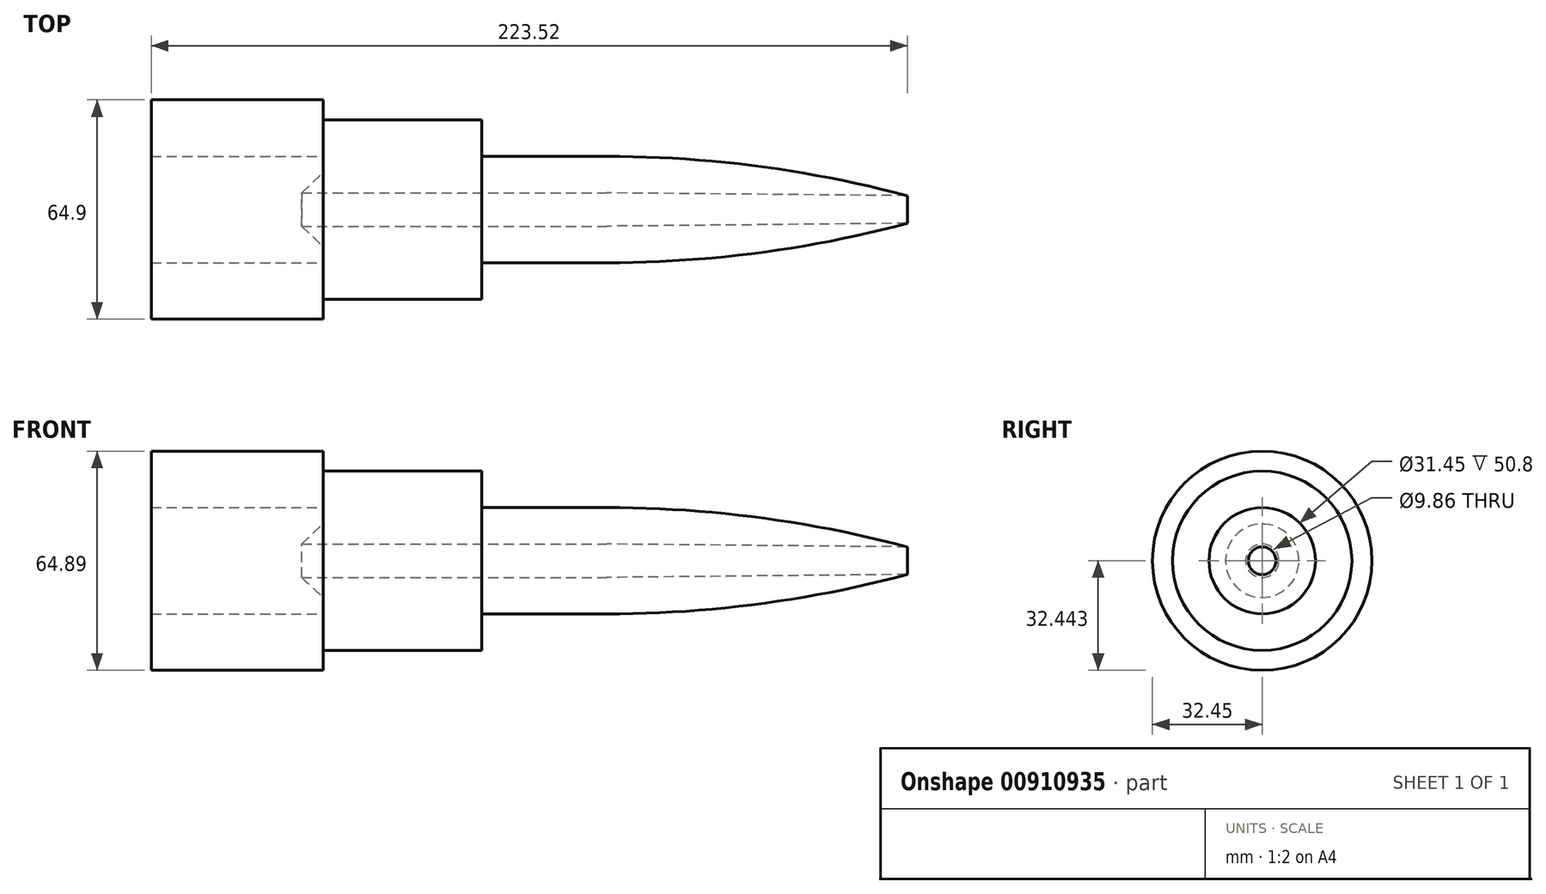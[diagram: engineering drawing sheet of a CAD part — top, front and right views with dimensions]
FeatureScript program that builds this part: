
annotation { "Feature Type Name" : "Feature", "Feature Type Description" : "" }
export const myFeature = defineFeature(function(context is Context, id is Id, definition is map)
    precondition{}
    {
        {
            var Q0;
            Q0=qCreatedBy(makeId("Front.planeOp"),FACE);
            var sketch = newSketch(context, id + "F0", { "sketchPlane" : qUnion([Q0])});
            skLineSegment(sketch, "E0.bottom", {"start": v(-57.4, 34.77) * mm, "end": v(-10.41, 34.77) * mm});
            skLineSegment(sketch, "E0.top", {"start": v(-57.4, 13.18) * mm, "end": v(-10.41, 13.18) * mm});
            skLineSegment(sketch, "E0.left", {"start": v(-57.4, 34.77) * mm, "end": v(-57.4, 13.18) * mm});
            skLineSegment(sketch, "E0.right", {"start": v(-10.41, 34.77) * mm, "end": v(-10.41, 13.18) * mm});
            skPoint(sketch, "E1.oppositeSnap0", {"position": v(-10.41, 23.98) * mm});
            skLineSegment(sketch, "E1.bottom", {"start": v(-10.41, 13.18) * mm, "end": v(26.41, 13.18) * mm});
            skLineSegment(sketch, "E1.top", {"start": v(-10.41, 23.98) * mm, "end": v(26.41, 23.98) * mm});
            skLineSegment(sketch, "E1.left", {"start": v(-10.41, 13.18) * mm, "end": v(-10.41, 23.98) * mm});
            skLineSegment(sketch, "E1.right", {"start": v(26.41, 13.18) * mm, "end": v(26.41, 23.98) * mm});
            skArc(sketch, "E2", {"start": v(26.41, 23.98) * mm, "mid": v(71.24, 21.06) * mm, "end": v(115.3, 12.34) * mm});
            skLineSegment(sketch, "E3", {"start": v(26.41, 13.18) * mm, "end": v(115.3, 12.34) * mm});
            skLineSegment(sketch, "E4.bottom", {"start": v(-57.4, 23.98) * mm, "end": v(-108.2, 23.98) * mm});
            skLineSegment(sketch, "E4.top", {"start": v(-57.4, 40.7) * mm, "end": v(-108.2, 40.7) * mm});
            skLineSegment(sketch, "E4.left", {"start": v(-57.4, 23.98) * mm, "end": v(-57.4, 40.7) * mm});
            skLineSegment(sketch, "E4.right", {"start": v(-108.2, 23.98) * mm, "end": v(-108.2, 40.7) * mm});
            skLineSegment(sketch, "E5", {"start": v(-63.76, 13.18) * mm, "end": v(-57.4, 19.11) * mm});
            skLineSegment(sketch, "E6", {"start": v(-63.76, 13.18) * mm, "end": v(-57.4, 13.18) * mm});
            skLineSegment(sketch, "E7", {"start": v(115.3, 8.25) * mm, "end": v(-109.11, 8.25) * mm});
            skSolve(sketch);
        }
        {
            var Q0;
            {var subQ3=sQuery(id+"F0.wireOp",EDGE,"E4.bottom");Q0=makeQuery(id+"F0.imprint","IMPRINT",FACE,{"disambiguationData":[TD([[makeQuery(id+"F0.imprint","IMPRINT",EDGE,{"derivedFrom":subQ3}),-1.0]])]});}
            var Q1;
            {var subQ5=sQuery(id+"F0.wireOp",EDGE,"E0.bottom");Q1=makeQuery(id+"F0.imprint","IMPRINT",FACE,{"disambiguationData":[TD([[makeQuery(id+"F0.imprint","IMPRINT",EDGE,{"derivedFrom":subQ5}),-1.0]])]});}
            var Q2;
            Q2=makeQuery(id+"F0.imprint","IMPRINT",FACE,{"disambiguationData":[TD([[makeQuery(id+"F0.imprint","IMPRINT",EDGE,{"derivedFrom":sQuery(id+"F0.wireOp",EDGE,"E1.bottom")}),1.0]])]});
            var Q3;
            Q3=makeQuery(id+"F0.imprint","IMPRINT",FACE,{"disambiguationData":[TD([[makeQuery(id+"F0.imprint","IMPRINT",EDGE,{"derivedFrom":sQuery(id+"F0.wireOp",EDGE,"E1.right")}),-1.0]])]});
            var Q4;
            {var subQ2=sQuery(id+"F0.wireOp",EDGE,"E5");Q4=makeQuery(id+"F0.imprint","IMPRINT",FACE,{"disambiguationData":[TD([[makeQuery(id+"F0.imprint","IMPRINT",EDGE,{"derivedFrom":subQ2}),-1.0]])]});}
            var Q5;
            Q5=sQuery(id+"F0.wireOp",EDGE,"E7");
            revolve(context, id + "F1", {"surfaceOperationType" : NewSurfaceOperationType.NEW, "entities" : qUnion([Q0, Q1, Q2, Q3, Q4]), "axis" : qUnion([Q5]), "revolveType" : RevolveType.FULL});
        }
    });
